# Revit family: Shower-Showerhead_Kit-KOHLER-PARALLEL-K-22645ME_1
name_source: partatom
category: Plumbing Fixtures
units: mm (PartAtom-declared; Revit-internal decimal feet)

## family parameters
Cut with Voids When Loaded = No
Host = Face
Maintain Annotation Orientation = No
OmniClass Number = 23.31.17.00
OmniClass Title = Showers
Part Type = Normal
Room Calculation Point = No
Round Connector Dimension = Use Diameter
Shared = No

## types (3) — shared parameters
ADA Compliant = No
Assembly Code = D2010700
CW Connection = No
Cold Water Inlet = Cold Water Inlet
Date Modified = 1/4/2023
Default Elevation = 72"
Description = Single Function Showerhead
Drain Included = No
Flow Rate = 3 GPM
HW Connection = Yes
Height = 2 3/8"
Hot Water Inlet = Hot Water Inlett
Length = 8 3/4"
Manufacturer = Kohler Co.
Master Format 2014 = 22 42 23
Master Format 2014 Name = Residential Showers
Material = Premium Metal Construction
Pressure = 45.00 psi
Product Documentation Link = https://me.kohler.com
Product Name = PARALLEL
Product Page URL = https://me.kohler.com
Tempered Water Inlet = Tempered Water Inlet
URL = https://me.kohler.com
Vent Connection = No
Waste Connection = No
Waste Water Outlet = Waste Water Outlet
WaterSense Certified = No
Width = 2 3/8"

## per-type parameters (varying)
| type | Finish | Model | Type |
| CP-Polished Chrome | Kohler-Metal-CP-Polished_Chrome | K-22645ME-CP | 3 |
| AF-Flange Gold | Kohler-Metal-AF-Flange_Gold | K-22645ME-AF | 1 |
| BN-Roman Silver | Kohler-Metal-BN-Roman_Silver | K-22645ME-BN | 2 |

## geometry (parser evidence)
native form markers: Sweep x5
no freeform markers — native parametric forms only
